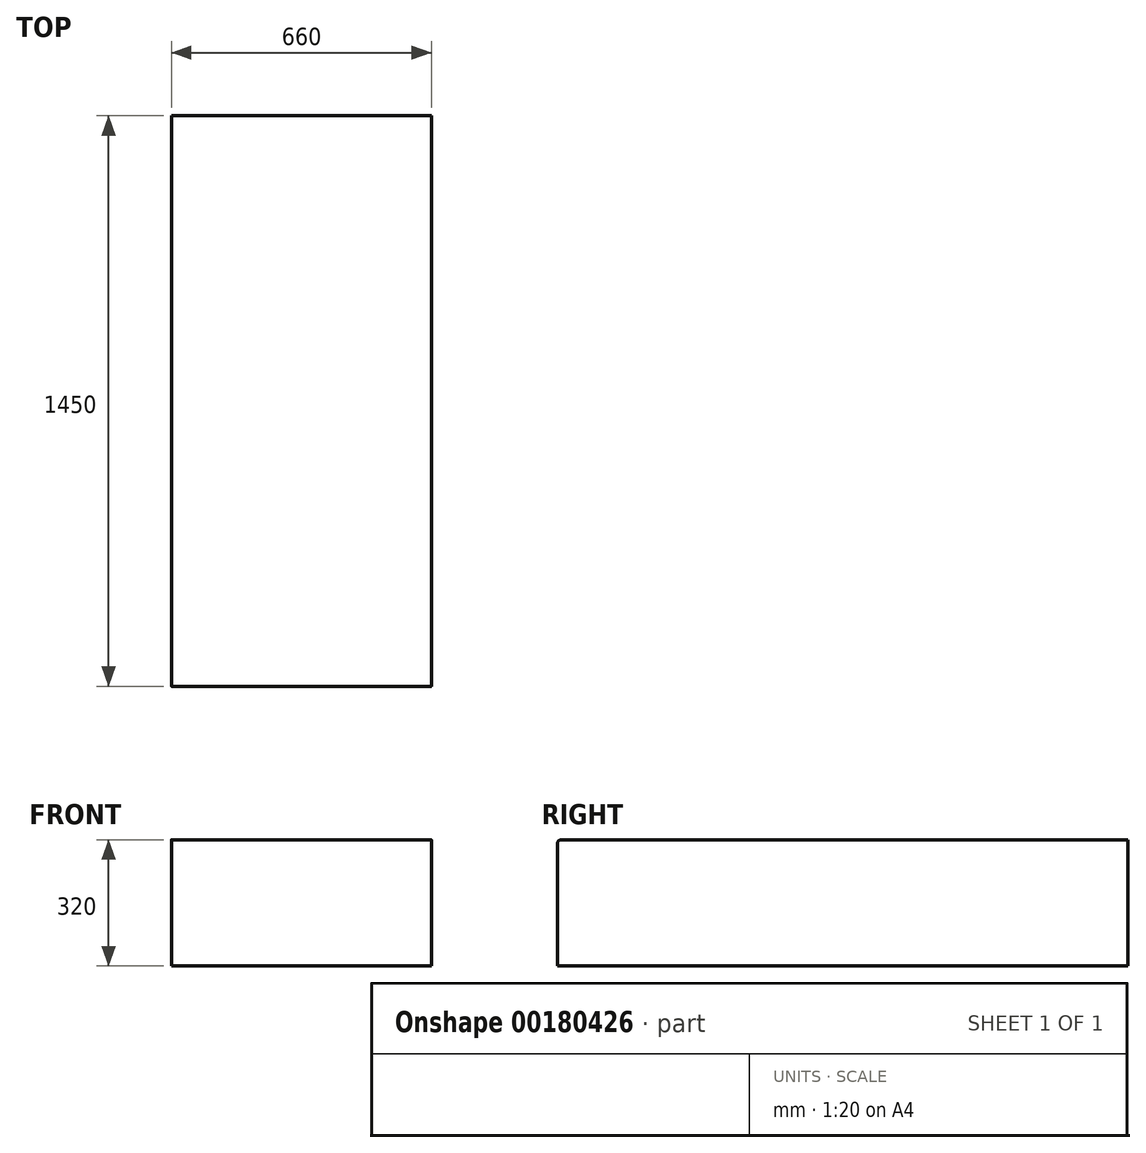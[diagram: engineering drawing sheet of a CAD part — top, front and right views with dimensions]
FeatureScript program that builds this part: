
annotation { "Feature Type Name" : "Feature", "Feature Type Description" : "" }
export const myFeature = defineFeature(function(context is Context, id is Id, definition is map)
    precondition{}
    {
        {
            var Q0;
            Q0=qCreatedBy(makeId("Top.planeOp"),FACE);
            var sketch = newSketch(context, id + "F0", { "sketchPlane" : qUnion([Q0])});
            skLineSegment(sketch, "E0.bottom", {"start": v(-304.62, 678.39) * mm, "end": v(355.38, 678.39) * mm});
            skLineSegment(sketch, "E0.top", {"start": v(-304.62, -771.61) * mm, "end": v(355.38, -771.61) * mm});
            skLineSegment(sketch, "E0.left", {"start": v(-304.62, 678.39) * mm, "end": v(-304.62, -771.61) * mm});
            skLineSegment(sketch, "E0.right", {"start": v(355.38, 678.39) * mm, "end": v(355.38, -771.61) * mm});
            skSolve(sketch);
        }
        {
            var Q0;
            Q0=makeQuery(id+"F0.imprint","IMPRINT",FACE,{"disambiguationData":[TD([[makeQuery(id+"F0.imprint","IMPRINT",EDGE,{"derivedFrom":sQuery(id+"F0.wireOp",EDGE,"E0.bottom")}),-1.0]])]});
            extrude(context, id + "F1", {"entities" : qUnion([Q0]), "depth" : 320 * mm});
        }
        {
            var Q0;
            Q0=makeQuery(id+"F1.opExtrude","CAP_EDGE",EDGE,{"disambiguationData":[OSD([sQuery(id+"F0.wireOp",EDGE,"E0.top")])],"isStart":false});
            fillet(context, id + "F2", {"entities" : qUnion([Q0]), "radius" : 10 * mm, "tangentPropagation" : true, "allowEdgeOverflow" : false});
        }
    });
